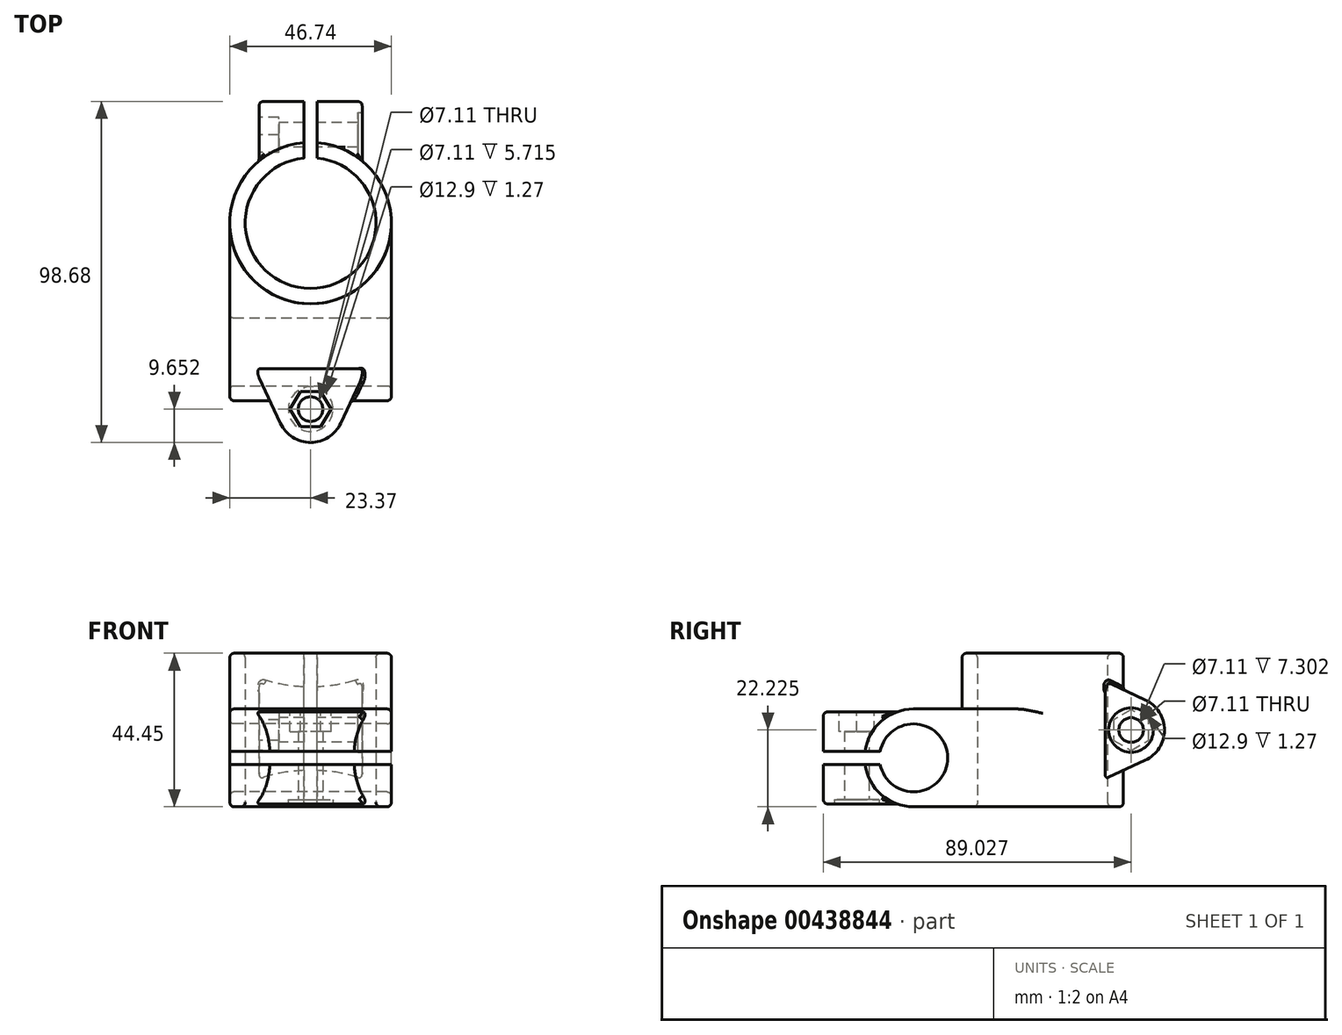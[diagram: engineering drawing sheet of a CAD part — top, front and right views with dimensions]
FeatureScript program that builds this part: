
annotation { "Feature Type Name" : "Feature", "Feature Type Description" : "" }
export const myFeature = defineFeature(function(context is Context, id is Id, definition is map)
    precondition{}
    {
        {
            var Q0;
            Q0=qCreatedBy(makeId("Top.planeOp"),FACE);
            var sketch = newSketch(context, id + "F0", { "sketchPlane" : qUnion([Q0])});
            skCircle(sketch, "E0", {"center": v(0, 0) * mm, "radius": 23.37 * mm});
            skCircle(sketch, "E1", {"center": v(0, 0) * mm, "radius": 18.92 * mm});
            skSolve(sketch);
        }
        {
            var Q0;
            Q0=qSketchRegion(id+"F0",true);
            extrude(context, id + "F1", {"entities" : qUnion([Q0]), "depth" : 44.45 * mm});
        }
        {
            var Q0;
            Q0=qCreatedBy(makeId("Right.planeOp"),FACE);
            var sketch = newSketch(context, id + "F2", { "sketchPlane" : qUnion([Q0])});
            skLineSegment(sketch, "E2.bottom", {"start": v(0, 0) * mm, "end": v(-37.4, 0) * mm});
            skLineSegment(sketch, "E2.top", {"start": v(0, 28.32) * mm, "end": v(-37.4, 28.32) * mm});
            skLineSegment(sketch, "E2.left", {"start": v(0, 0) * mm, "end": v(0, 28.32) * mm});
            skArc(sketch, "E3", {"start": v(-37.4, 28.32) * mm, "mid": v(-51.56, 14.16) * mm, "end": v(-37.4, 0) * mm});
            skCircle(sketch, "E4", {"center": v(-37.4, 14.16) * mm, "radius": 9.84 * mm});
            skPoint(sketch, "E5", {"position": v(-51.56, 14.16) * mm});
            skLineSegment(sketch, "E6.0", {"start": v(-23.37, 0) * mm, "end": v(23.37, 0) * mm, "construction": true});
            skSolve(sketch);
        }
        {
            var Q0;
            Q0=makeQuery(id+"F2.imprint","IMPRINT",FACE,{"disambiguationData":[TD([[makeQuery(id+"F2.imprint","IMPRINT",EDGE,{"derivedFrom":sQuery(id+"F2.wireOp",EDGE,"E2.bottom")}),-1.0]])]});
            extrude(context, id + "F3", {"entities" : qUnion([Q0]), "operationType" : NewBodyOperationType.ADD, "endBound" : BoundingType.SYMMETRIC, "depth" : 46.74 * mm});
        }
        {
            var Q0;
            Q0=qCreatedBy(makeId("Right.planeOp"),FACE);
            var sketch = newSketch(context, id + "F4", { "sketchPlane" : qUnion([Q0])});
            skLineSegment(sketch, "E7", {"start": v(0, -0.33) * mm, "end": v(29.6, 13.48) * mm});
            skLineSegment(sketch, "E8", {"start": v(29.6, 30.97) * mm, "end": v(0, 44.78) * mm});
            skArc(sketch, "E9", {"start": v(29.6, 13.48) * mm, "mid": v(35.18, 22.23) * mm, "end": v(29.6, 30.97) * mm});
            skLineSegment(sketch, "E10", {"start": v(0, -0.33) * mm, "end": v(0, 44.78) * mm});
            skCircle(sketch, "E11", {"center": v(25.53, 22.23) * mm, "radius": 3.56 * mm});
            skLineSegment(sketch, "E12.0", {"start": v(-18.92, 44.45) * mm, "end": v(18.92, 44.45) * mm, "construction": true});
            skPoint(sketch, "E13", {"position": v(35.18, 22.23) * mm});
            skLineSegment(sketch, "E14", {"start": v(0, 0) * mm, "end": v(0, 44.45) * mm, "construction": true});
            skPoint(sketch, "E15", {"position": v(0, 22.23) * mm});
            skSolve(sketch);
        }
        {
            var Q0;
            Q0=qSketchRegion(id+"F4",true);
            extrude(context, id + "F5", {"entities" : qUnion([Q0]), "operationType" : NewBodyOperationType.ADD, "endBound" : BoundingType.SYMMETRIC, "depth" : 29.84 * mm});
        }
        {
            var Q0;
            {var subQ3=sQuery(id+"F2.wireOp",EDGE,"E2.top");Q0=makeQuery(id+"F3.boolean.opBoolean","SPLIT",FACE,{"disambiguationData":[TD([makeQuery(id+"F1.opExtrude","SWEPT_FACE",FACE,{"disambiguationData":[OSD([sQuery(id+"F0.wireOp",EDGE,"E0")])]})])],"derivedFrom":makeQuery(id+"F3.opExtrude","SWEPT_FACE",FACE,{"disambiguationData":[OSD([subQ3])]})});}
            var Q1;
            Q1=makeQuery(id+"F3.boolean.opBoolean","MERGE",FACE,{"derivedFrom":[makeQuery(id+"F1.opExtrude","CAP_FACE",FACE,{"disambiguationData":[OSD([sQuery(id+"F0.wireOp",EDGE,"E0"),sQuery(id+"F0.wireOp",EDGE,"E1")])],"isStart":true}),makeQuery(id+"F3.opExtrude","SWEPT_FACE",FACE,{"disambiguationData":[OSD([sQuery(id+"F2.wireOp",EDGE,"E2.bottom")])]})]});
            cPlane(context, id + "F6", {"entities" : qUnion([Q0, Q1]), "cplaneType" : CPlaneType.MID_PLANE, "offset" : 25.4 * mm, "width" : 152.4 * mm, "height" : 152.4 * mm});
        }
        {
            var Q0;
            Q0=qCreatedBy(id+"F6.planeOp",FACE);
            var sketch = newSketch(context, id + "F7", { "sketchPlane" : qUnion([Q0])});
            skLineSegment(sketch, "E16", {"start": v(-23.37, -26.57) * mm, "end": v(-8.75, -57.93) * mm});
            skLineSegment(sketch, "E17", {"start": v(8.75, -57.93) * mm, "end": v(23.37, -26.57) * mm});
            skArc(sketch, "E18", {"start": v(-8.75, -57.93) * mm, "mid": v(0, -63.5) * mm, "end": v(8.75, -57.93) * mm});
            skLineSegment(sketch, "E19", {"start": v(-23.37, -26.57) * mm, "end": v(23.37, -26.57) * mm});
            skCircle(sketch, "E20", {"center": v(0, -53.85) * mm, "radius": 3.56 * mm});
            skPoint(sketch, "E21", {"position": v(0, -63.5) * mm});
            skLineSegment(sketch, "E22.0", {"start": v(23.37, -27.56) * mm, "end": v(23.37, -47.24) * mm, "construction": true});
            skSolve(sketch);
        }
        {
            var Q0;
            Q0=qSketchRegion(id+"F7",true);
            extrude(context, id + "F8", {"entities" : qUnion([Q0]), "operationType" : NewBodyOperationType.ADD, "endBound" : BoundingType.SYMMETRIC, "depth" : 26.67 * mm});
        }
        {
            var Q0;
            {var subQ0=sQuery(id+"F4.wireOp",EDGE,"E9");var subQ1=sQuery(id+"F4.wireOp",EDGE,"E7");var subQ2=sQuery(id+"F4.wireOp",EDGE,"E8");var subQ3=sQuery(id+"F4.wireOp",EDGE,"E11");Q0=makeQuery(id+"F5.boolean.opBoolean","SPLIT",FACE,{"disambiguationData":[TD([makeQuery(id+"F1.opExtrude","SWEPT_FACE",FACE,{"disambiguationData":[OSD([sQuery(id+"F0.wireOp",EDGE,"E0")])]})])],"derivedFrom":makeQuery(id+"F5.opExtrude","CAP_FACE",FACE,{"disambiguationData":[OSD([subQ1,subQ2,subQ0,sQuery(id+"F4.wireOp",EDGE,"E10"),subQ3])],"isStart":false})});}
            var sketch = newSketch(context, id + "F9", { "sketchPlane" : qUnion([Q0])});
            skCircle(sketch, "E23.0", {"center": v(25.53, 22.23) * mm, "radius": 3.56 * mm});
            skSolve(sketch);
        }
        {
            var Q0;
            Q0=qSketchRegion(id+"F9",true);
            extrude(context, id + "F10", {"entities" : qUnion([Q0]), "operationType" : NewBodyOperationType.REMOVE, "endBound" : BoundingType.THROUGH_ALL, "oppositeDirection" : true, "depth" : 25.4 * mm});
        }
        {
            var Q0;
            Q0=makeQuery(id+"F1.opExtrude","CAP_FACE",FACE,{"disambiguationData":[OSD([sQuery(id+"F0.wireOp",EDGE,"E0"),sQuery(id+"F0.wireOp",EDGE,"E1")])],"isStart":false});
            var sketch = newSketch(context, id + "F11", { "sketchPlane" : qUnion([Q0])});
            skCircle(sketch, "E24.0", {"center": v(0, 0) * mm, "radius": 18.92 * mm});
            skLineSegment(sketch, "E25.bottom", {"start": v(-1.9, 17.3) * mm, "end": v(1.9, 17.3) * mm});
            skLineSegment(sketch, "E25.top", {"start": v(-1.9, 38.21) * mm, "end": v(1.9, 38.21) * mm});
            skLineSegment(sketch, "E25.left", {"start": v(-1.9, 17.3) * mm, "end": v(-1.9, 38.21) * mm});
            skLineSegment(sketch, "E25.right", {"start": v(1.9, 17.3) * mm, "end": v(1.9, 38.21) * mm});
            skPoint(sketch, "E26", {"position": v(0, 17.3) * mm});
            skSolve(sketch);
        }
        {
            var Q0;
            Q0=qSketchRegion(id+"F11",true);
            extrude(context, id + "F12", {"entities" : qUnion([Q0]), "operationType" : NewBodyOperationType.REMOVE, "endBound" : BoundingType.THROUGH_ALL, "oppositeDirection" : true, "depth" : 25.4 * mm, "hasSecondDirection" : true, "secondDirectionBound" : SecondDirectionBoundingType.THROUGH_ALL, "secondDirectionOppositeDirection" : false, "secondDirectionDepth" : 25.4 * mm});
        }
        {
            var Q0;
            Q0=makeQuery(id+"F3.opExtrude","CAP_FACE",FACE,{"disambiguationData":[OSD([sQuery(id+"F2.wireOp",EDGE,"E2.bottom"),sQuery(id+"F2.wireOp",EDGE,"E2.top"),sQuery(id+"F2.wireOp",EDGE,"E2.left"),sQuery(id+"F2.wireOp",EDGE,"E3"),sQuery(id+"F2.wireOp",EDGE,"E4")])],"isStart":false});
            var sketch = newSketch(context, id + "F13", { "sketchPlane" : qUnion([Q0])});
            skCircle(sketch, "E27.0", {"center": v(-37.4, 14.16) * mm, "radius": 9.84 * mm});
            skLineSegment(sketch, "E28.bottom", {"start": v(-45.86, 16.07) * mm, "end": v(-64.41, 16.07) * mm});
            skLineSegment(sketch, "E28.top", {"start": v(-45.86, 12.26) * mm, "end": v(-64.41, 12.26) * mm});
            skLineSegment(sketch, "E28.left", {"start": v(-45.86, 16.07) * mm, "end": v(-45.86, 12.26) * mm});
            skLineSegment(sketch, "E28.right", {"start": v(-64.41, 16.07) * mm, "end": v(-64.41, 12.26) * mm});
            skPoint(sketch, "E29", {"position": v(-45.86, 14.16) * mm});
            skSolve(sketch);
        }
        {
            var Q0;
            Q0=qSketchRegion(id+"F13",true);
            extrude(context, id + "F14", {"entities" : qUnion([Q0]), "operationType" : NewBodyOperationType.REMOVE, "endBound" : BoundingType.THROUGH_ALL, "oppositeDirection" : true, "depth" : 25.4 * mm});
        }
        {
            var Q0;
            Q0=makeQuery(id+"F8.opExtrude","CAP_FACE",FACE,{"disambiguationData":[OSD([sQuery(id+"F7.wireOp",EDGE,"E16"),sQuery(id+"F7.wireOp",EDGE,"E17"),sQuery(id+"F7.wireOp",EDGE,"E18"),sQuery(id+"F7.wireOp",EDGE,"E19"),sQuery(id+"F7.wireOp",EDGE,"E20")])],"isStart":false});
            var sketch = newSketch(context, id + "F15", { "sketchPlane" : qUnion([Q0])});
            skCircle(sketch, "E30.0", {"center": v(0, -53.85) * mm, "radius": 3.56 * mm});
            skSolve(sketch);
        }
        {
            var Q0;
            Q0=qSketchRegion(id+"F15",true);
            extrude(context, id + "F16", {"entities" : qUnion([Q0]), "operationType" : NewBodyOperationType.REMOVE, "endBound" : BoundingType.THROUGH_ALL, "oppositeDirection" : true, "depth" : 25.4 * mm});
        }
        {
            var Q0;
            Q0=makeQuery(id+"F8.opExtrude","CAP_FACE",FACE,{"disambiguationData":[OSD([sQuery(id+"F7.wireOp",EDGE,"E16"),sQuery(id+"F7.wireOp",EDGE,"E17"),sQuery(id+"F7.wireOp",EDGE,"E18"),sQuery(id+"F7.wireOp",EDGE,"E19"),sQuery(id+"F7.wireOp",EDGE,"E20")])],"isStart":false});
            var sketch = newSketch(context, id + "F17", { "sketchPlane" : qUnion([Q0])});
            skCircle(sketch, "E31.cCircle", {"center": v(0, -53.85) * mm, "radius": 5.13 * mm, "construction": true});
            skLineSegment(sketch, "E31.0", {"start": v(2.96, -58.98) * mm, "end": v(-2.96, -58.98) * mm});
            skLineSegment(sketch, "E31.1", {"start": v(-2.96, -58.98) * mm, "end": v(-5.92, -53.85) * mm});
            skLineSegment(sketch, "E31.2", {"start": v(-5.92, -53.85) * mm, "end": v(-2.96, -48.72) * mm});
            skLineSegment(sketch, "E31.3", {"start": v(-2.96, -48.72) * mm, "end": v(2.96, -48.72) * mm});
            skLineSegment(sketch, "E31.4", {"start": v(2.96, -48.72) * mm, "end": v(5.92, -53.85) * mm});
            skLineSegment(sketch, "E31.5", {"start": v(5.92, -53.85) * mm, "end": v(2.96, -58.98) * mm});
            skPoint(sketch, "E31.0.midPoint", {"position": v(0, -58.98) * mm});
            skSolve(sketch);
        }
        {
            var Q0;
            Q0=qSketchRegion(id+"F17",true);
            extrude(context, id + "F18", {"entities" : qUnion([Q0]), "operationType" : NewBodyOperationType.REMOVE, "oppositeDirection" : true, "depth" : 5.7 * mm});
        }
        {
            var Q0;
            Q0=makeQuery(id+"F8.opExtrude","CAP_FACE",FACE,{"disambiguationData":[OSD([sQuery(id+"F7.wireOp",EDGE,"E16"),sQuery(id+"F7.wireOp",EDGE,"E17"),sQuery(id+"F7.wireOp",EDGE,"E18"),sQuery(id+"F7.wireOp",EDGE,"E19"),sQuery(id+"F7.wireOp",EDGE,"E20")])],"isStart":true});
            var sketch = newSketch(context, id + "F19", { "sketchPlane" : qUnion([Q0])});
            skCircle(sketch, "E32", {"center": v(0, 53.85) * mm, "radius": 6.45 * mm});
            skSolve(sketch);
        }
        {
            var Q0;
            Q0=qSketchRegion(id+"F19",true);
            extrude(context, id + "F20", {"entities" : qUnion([Q0]), "operationType" : NewBodyOperationType.REMOVE, "oppositeDirection" : true, "depth" : 1.27 * mm});
        }
        {
            var Q0;
            {var subQ0=sQuery(id+"F4.wireOp",EDGE,"E9");var subQ1=sQuery(id+"F4.wireOp",EDGE,"E7");var subQ2=sQuery(id+"F4.wireOp",EDGE,"E8");var subQ3=sQuery(id+"F4.wireOp",EDGE,"E11");Q0=makeQuery(id+"F5.boolean.opBoolean","SPLIT",FACE,{"disambiguationData":[TD([makeQuery(id+"F1.opExtrude","SWEPT_FACE",FACE,{"disambiguationData":[OSD([sQuery(id+"F0.wireOp",EDGE,"E0")])]})])],"derivedFrom":makeQuery(id+"F5.opExtrude","CAP_FACE",FACE,{"disambiguationData":[OSD([subQ1,subQ2,subQ0,sQuery(id+"F4.wireOp",EDGE,"E10"),subQ3])],"isStart":false})});}
            var sketch = newSketch(context, id + "F21", { "sketchPlane" : qUnion([Q0])});
            skCircle(sketch, "E33", {"center": v(25.53, 22.23) * mm, "radius": 6.45 * mm});
            skSolve(sketch);
        }
        {
            var Q0;
            Q0=makeQuery(id+"F21.imprint","IMPRINT",FACE,{"disambiguationData":[TD([[makeQuery(id+"F21.imprint","IMPRINT",EDGE,{"derivedFrom":sQuery(id+"F21.wireOp",EDGE,"E33")}),1.0]])]});
            var Q1;
            Q1=qSketchRegion(id+"F21",true);
            extrude(context, id + "F22", {"entities" : qUnion([Q0, Q1]), "operationType" : NewBodyOperationType.REMOVE, "oppositeDirection" : true, "depth" : 1.27 * mm});
        }
        {
            var Q0;
            {var subQ0=sQuery(id+"F4.wireOp",EDGE,"E9");var subQ1=sQuery(id+"F4.wireOp",EDGE,"E7");var subQ2=sQuery(id+"F4.wireOp",EDGE,"E8");var subQ3=sQuery(id+"F4.wireOp",EDGE,"E11");Q0=makeQuery(id+"F5.boolean.opBoolean","SPLIT",FACE,{"disambiguationData":[TD([makeQuery(id+"F1.opExtrude","SWEPT_FACE",FACE,{"disambiguationData":[OSD([sQuery(id+"F0.wireOp",EDGE,"E0")])]})])],"derivedFrom":makeQuery(id+"F5.opExtrude","CAP_FACE",FACE,{"disambiguationData":[OSD([subQ1,subQ2,subQ0,sQuery(id+"F4.wireOp",EDGE,"E10"),subQ3])],"isStart":true})});}
            var sketch = newSketch(context, id + "F23", { "sketchPlane" : qUnion([Q0])});
            skCircle(sketch, "E34.cCircle", {"center": v(-25.53, 22.23) * mm, "radius": 5.13 * mm, "construction": true});
            skLineSegment(sketch, "E34.0", {"start": v(-30.66, 19.26) * mm, "end": v(-30.66, 25.19) * mm});
            skLineSegment(sketch, "E34.1", {"start": v(-30.66, 25.19) * mm, "end": v(-25.53, 28.15) * mm});
            skLineSegment(sketch, "E34.2", {"start": v(-25.53, 28.15) * mm, "end": v(-20.4, 25.19) * mm});
            skLineSegment(sketch, "E34.3", {"start": v(-20.4, 25.19) * mm, "end": v(-20.4, 19.26) * mm});
            skLineSegment(sketch, "E34.4", {"start": v(-20.4, 19.26) * mm, "end": v(-25.53, 16.3) * mm});
            skLineSegment(sketch, "E34.5", {"start": v(-25.53, 16.3) * mm, "end": v(-30.66, 19.26) * mm});
            skPoint(sketch, "E34.0.midPoint", {"position": v(-30.66, 22.23) * mm});
            skSolve(sketch);
        }
        {
            var Q0;
            Q0=qSketchRegion(id+"F23",true);
            extrude(context, id + "F24", {"entities" : qUnion([Q0]), "operationType" : NewBodyOperationType.REMOVE, "oppositeDirection" : true, "depth" : 5.7 * mm});
        }
        {
            var Q0;
            Q0=makeQuery(id+"F3.opExtrude","CAP_EDGE",EDGE,{"disambiguationData":[OSD([sQuery(id+"F2.wireOp",EDGE,"E4")])],"isStart":true});
            var Q1;
            Q1=makeQuery(id+"F3.opExtrude","CAP_EDGE",EDGE,{"disambiguationData":[OSD([sQuery(id+"F2.wireOp",EDGE,"E2.bottom")])],"isStart":true});
            var Q2;
            {var subQ0=sQuery(id+"F2.wireOp",EDGE,"E3");var subQ1=sQuery(id+"F2.wireOp",EDGE,"E2.bottom");Q2=makeQuery(id+"F14.boolean.opBoolean","SPLIT",EDGE,{"disambiguationData":[TD([makeQuery(id+"F3.opExtrude","SWEPT_FACE",FACE,{"disambiguationData":[OSD([subQ1])]})])],"derivedFrom":makeQuery(id+"F3.opExtrude","CAP_EDGE",EDGE,{"disambiguationData":[OSD([subQ0])],"isStart":true})});}
            var Q3;
            Q3=makeQuery(id+"F3.opExtrude","CAP_EDGE",EDGE,{"disambiguationData":[OSD([sQuery(id+"F2.wireOp",EDGE,"E2.top")])],"isStart":false});
            var Q4;
            {var subQ0=sQuery(id+"F2.wireOp",EDGE,"E3");var subQ1=sQuery(id+"F2.wireOp",EDGE,"E2.top");Q4=makeQuery(id+"F14.boolean.opBoolean","SPLIT",EDGE,{"disambiguationData":[TD([makeQuery(id+"F3.opExtrude","SWEPT_FACE",FACE,{"disambiguationData":[OSD([subQ1])]})])],"derivedFrom":makeQuery(id+"F3.opExtrude","CAP_EDGE",EDGE,{"disambiguationData":[OSD([subQ0])],"isStart":false})});}
            var Q5;
            Q5=makeQuery(id+"F3.opExtrude","CAP_EDGE",EDGE,{"disambiguationData":[OSD([sQuery(id+"F2.wireOp",EDGE,"E2.bottom")])],"isStart":false});
            var Q6;
            Q6=makeQuery(id+"F3.opExtrude","CAP_EDGE",EDGE,{"disambiguationData":[OSD([sQuery(id+"F2.wireOp",EDGE,"E4")])],"isStart":false});
            var Q7;
            Q7=makeQuery(id+"F1.opExtrude","CAP_EDGE",EDGE,{"disambiguationData":[OSD([sQuery(id+"F0.wireOp",EDGE,"E0")])],"isStart":false});
            var Q8;
            Q8=makeQuery(id+"F1.opExtrude","CAP_EDGE",EDGE,{"disambiguationData":[OSD([sQuery(id+"F0.wireOp",EDGE,"E1")])],"isStart":false});
            var Q9;
            {var subQ0=sQuery(id+"F4.wireOp",EDGE,"E8");Q9=makeQuery(id+"F5.boolean.opBoolean","SPLIT",EDGE,{"disambiguationData":[TD([makeQuery(id+"F1.opExtrude","SWEPT_FACE",FACE,{"disambiguationData":[OSD([sQuery(id+"F0.wireOp",EDGE,"E0")])]})])],"derivedFrom":makeQuery(id+"F5.opExtrude","CAP_EDGE",EDGE,{"disambiguationData":[OSD([subQ0])],"isStart":false})});}
            var Q10;
            Q10=makeQuery(id+"F5.opExtrude","CAP_EDGE",EDGE,{"disambiguationData":[OSD([sQuery(id+"F4.wireOp",EDGE,"E9")])],"isStart":true});
            var Q11;
            {var subQ0=makeQuery(id+"F1.opExtrude","SWEPT_FACE",FACE,{"disambiguationData":[OSD([sQuery(id+"F0.wireOp",EDGE,"E0")])]});var subQ1=sQuery(id+"F4.wireOp",EDGE,"E8");var subQ2=makeQuery(id+"F5.opExtrude","SWEPT_FACE",FACE,{"disambiguationData":[OSD([subQ1])]});Q11=makeQuery(id+"F12.boolean.opBoolean","SPLIT",EDGE,{"disambiguationData":[TD([makeQuery(id+"F12.opExtrude","SWEPT_FACE",FACE,{"disambiguationData":[OSD([sQuery(id+"F11.wireOp",EDGE,"E25.right")])]})])],"derivedFrom":makeQuery(id+"F5.boolean.opBoolean","INTERSECT",EDGE,{"derivedFrom":[subQ0,subQ2]})});}
            var Q12;
            {var subQ0=makeQuery(id+"F1.opExtrude","SWEPT_FACE",FACE,{"disambiguationData":[OSD([sQuery(id+"F0.wireOp",EDGE,"E0")])]});var subQ1=sQuery(id+"F4.wireOp",EDGE,"E8");var subQ2=makeQuery(id+"F5.opExtrude","SWEPT_FACE",FACE,{"disambiguationData":[OSD([subQ1])]});Q12=makeQuery(id+"F12.boolean.opBoolean","SPLIT",EDGE,{"disambiguationData":[TD([makeQuery(id+"F12.opExtrude","SWEPT_FACE",FACE,{"disambiguationData":[OSD([sQuery(id+"F11.wireOp",EDGE,"E25.left")])]})])],"derivedFrom":makeQuery(id+"F5.boolean.opBoolean","INTERSECT",EDGE,{"derivedFrom":[subQ0,subQ2]})});}
            var Q13;
            Q13=makeQuery(id+"F12.boolean.opBoolean","INTERSECT",EDGE,{"derivedFrom":[makeQuery(id+"F3.boolean.opBoolean","MERGE",FACE,{"derivedFrom":[makeQuery(id+"F1.opExtrude","CAP_FACE",FACE,{"disambiguationData":[OSD([sQuery(id+"F0.wireOp",EDGE,"E0"),sQuery(id+"F0.wireOp",EDGE,"E1")])],"isStart":true}),makeQuery(id+"F3.opExtrude","SWEPT_FACE",FACE,{"disambiguationData":[OSD([sQuery(id+"F2.wireOp",EDGE,"E2.bottom")])]})]}),makeQuery(id+"F12.opExtrude","SWEPT_FACE",FACE,{"disambiguationData":[OSD([sQuery(id+"F11.wireOp",EDGE,"E24.0")])]})]});
            var Q14;
            Q14=makeQuery(id+"F3.opExtrude","CAP_EDGE",EDGE,{"disambiguationData":[OSD([sQuery(id+"F2.wireOp",EDGE,"E2.top")])],"isStart":true});
            var Q15;
            Q15=makeQuery(id+"F8.opExtrude","CAP_EDGE",EDGE,{"disambiguationData":[OSD([sQuery(id+"F7.wireOp",EDGE,"E18")])],"isStart":false});
            var Q16;
            Q16=makeQuery(id+"F8.opExtrude","CAP_EDGE",EDGE,{"disambiguationData":[OSD([sQuery(id+"F7.wireOp",EDGE,"E18")])],"isStart":true});
            var Q17;
            {var subQ0=makeQuery(id+"F3.opExtrude","SWEPT_FACE",FACE,{"disambiguationData":[OSD([sQuery(id+"F2.wireOp",EDGE,"E3")])]});var subQ1=sQuery(id+"F7.wireOp",EDGE,"E17");var subQ2=makeQuery(id+"F8.opExtrude","SWEPT_FACE",FACE,{"disambiguationData":[OSD([subQ1])]});Q17=makeQuery(id+"F14.boolean.opBoolean","SPLIT",EDGE,{"disambiguationData":[TD([makeQuery(id+"F14.opExtrude","SWEPT_FACE",FACE,{"disambiguationData":[OSD([sQuery(id+"F13.wireOp",EDGE,"E28.bottom")])]})])],"derivedFrom":makeQuery(id+"F8.boolean.opBoolean","INTERSECT",EDGE,{"derivedFrom":[subQ0,subQ2]})});}
            var Q18;
            {var subQ0=makeQuery(id+"F3.opExtrude","SWEPT_FACE",FACE,{"disambiguationData":[OSD([sQuery(id+"F2.wireOp",EDGE,"E3")])]});var subQ1=sQuery(id+"F7.wireOp",EDGE,"E17");var subQ2=makeQuery(id+"F8.opExtrude","SWEPT_FACE",FACE,{"disambiguationData":[OSD([subQ1])]});Q18=makeQuery(id+"F14.boolean.opBoolean","SPLIT",EDGE,{"disambiguationData":[TD([makeQuery(id+"F14.opExtrude","SWEPT_FACE",FACE,{"disambiguationData":[OSD([sQuery(id+"F13.wireOp",EDGE,"E28.top")])]})])],"derivedFrom":makeQuery(id+"F8.boolean.opBoolean","INTERSECT",EDGE,{"derivedFrom":[subQ0,subQ2]})});}
            fillet(context, id + "F25", {"entities" : qUnion([Q0, Q1, Q2, Q3, Q4, Q5, Q6, Q7, Q8, Q9, Q10, Q11, Q12, Q13, Q14, Q15, Q16, Q17, Q18]), "radius" : 1.27 * mm, "tangentPropagation" : true, "allowEdgeOverflow" : false});
        }
    });
